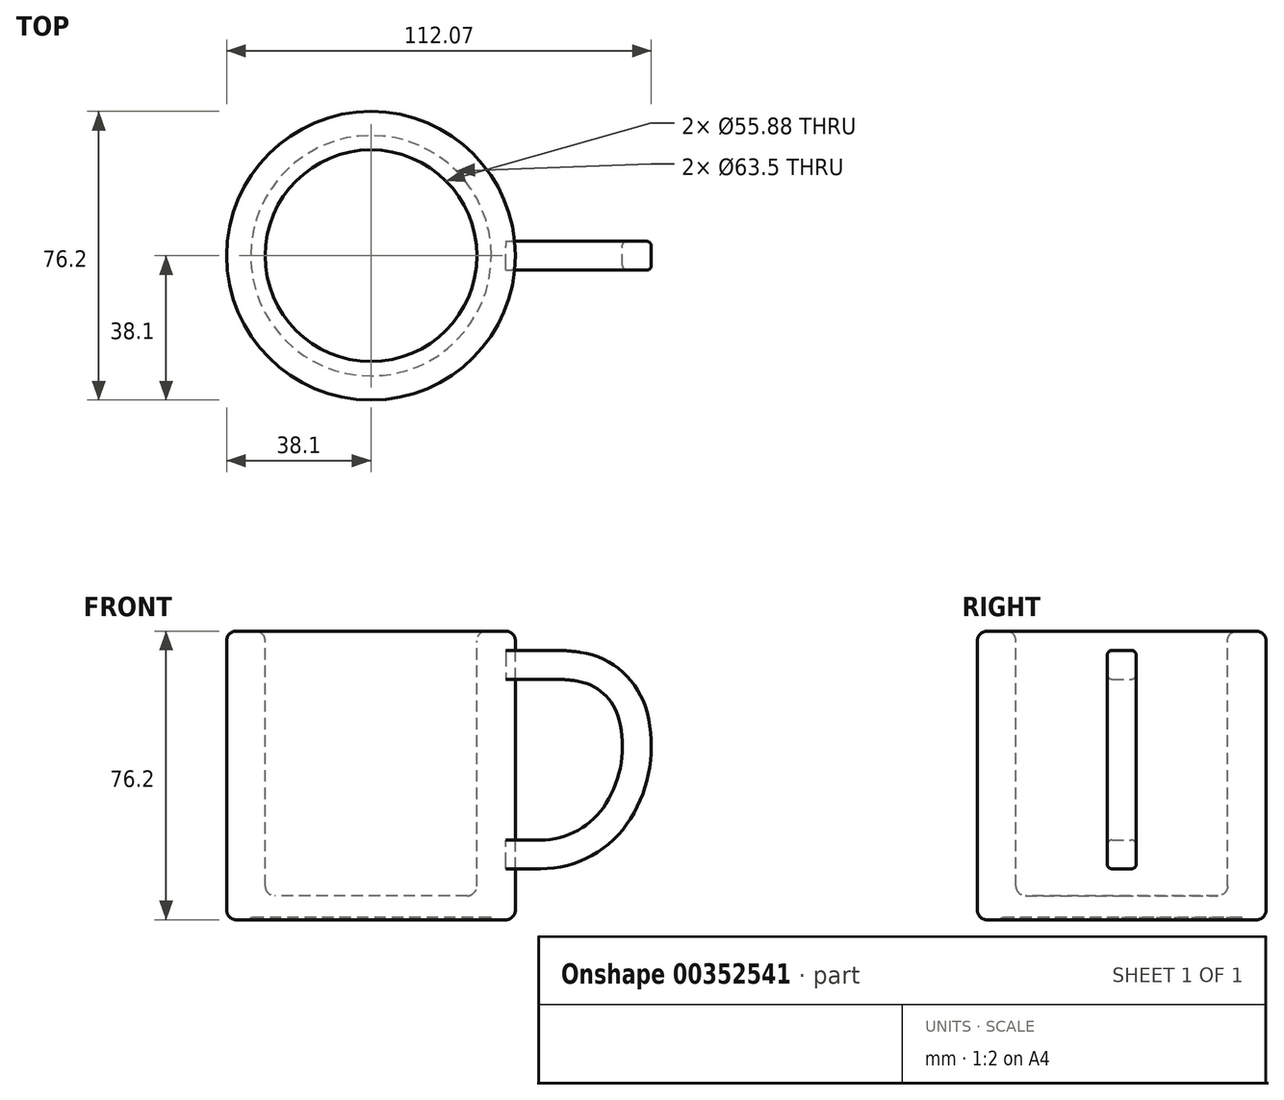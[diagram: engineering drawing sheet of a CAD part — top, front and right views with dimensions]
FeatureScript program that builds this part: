
annotation { "Feature Type Name" : "Feature", "Feature Type Description" : "" }
export const myFeature = defineFeature(function(context is Context, id is Id, definition is map)
    precondition{}
    {
        {
            var Q0;
            Q0=qCreatedBy(makeId("Front.planeOp"),FACE);
            var sketch = newSketch(context, id + "F0", { "sketchPlane" : qUnion([Q0])});
            skLineSegment(sketch, "E0.bottom", {"start": v(30.48, 76.2) * mm, "end": v(35.56, 76.2) * mm});
            skLineSegment(sketch, "E0.top", {"start": v(32, 0) * mm, "end": v(35.56, 0) * mm});
            skLineSegment(sketch, "E0.left", {"start": v(0, 6.35) * mm, "end": v(0, 0) * mm});
            skLineSegment(sketch, "E0.right", {"start": v(38.1, 73.66) * mm, "end": v(38.1, 2.54) * mm});
            skLineSegment(sketch, "E1.top", {"start": v(0, 6.35) * mm, "end": v(25.4, 6.35) * mm});
            skLineSegment(sketch, "E1.right", {"start": v(27.94, 73.66) * mm, "end": v(27.94, 8.9) * mm});
            skPoint(sketch, "E2.visualSharp", {"position": v(27.94, 6.35) * mm});
            skArc(sketch, "E2.filletArc", {"start": v(25.4, 6.35) * mm, "mid": v(27.2, 7.1) * mm, "end": v(27.94, 8.9) * mm});
            skPoint(sketch, "E3.visualSharp", {"position": v(27.94, 76.2) * mm});
            skArc(sketch, "E3.filletArc", {"start": v(30.48, 76.2) * mm, "mid": v(28.68, 75.46) * mm, "end": v(27.94, 73.66) * mm});
            skPoint(sketch, "E4.visualSharp", {"position": v(38.1, 76.2) * mm});
            skArc(sketch, "E4.filletArc", {"start": v(38.1, 73.66) * mm, "mid": v(37.36, 75.46) * mm, "end": v(35.56, 76.2) * mm});
            skPoint(sketch, "E5.visualSharp", {"position": v(38.1, 0) * mm});
            skArc(sketch, "E5.filletArc", {"start": v(35.56, 0) * mm, "mid": v(37.36, 0.74) * mm, "end": v(38.1, 2.54) * mm});
            skLineSegment(sketch, "E6.top", {"start": v(0, 0.64) * mm, "end": v(31.5, 0.64) * mm});
            skLineSegment(sketch, "E6.right", {"start": v(31.75, 0.25) * mm, "end": v(31.75, 0.38) * mm});
            skPoint(sketch, "E7.visualSharp", {"position": v(31.75, 0.64) * mm});
            skArc(sketch, "E7.filletArc", {"start": v(31.75, 0.38) * mm, "mid": v(31.67, 0.56) * mm, "end": v(31.5, 0.64) * mm});
            skPoint(sketch, "E8.visualSharp", {"position": v(31.75, 0) * mm});
            skArc(sketch, "E8.filletArc", {"start": v(31.75, 0.25) * mm, "mid": v(31.82, 0.07) * mm, "end": v(32, 0) * mm});
            skSolve(sketch);
        }
        {
            var Q0;
            Q0=makeQuery(id+"F0.imprint","IMPRINT",FACE,{"disambiguationData":[TD([[makeQuery(id+"F0.imprint","IMPRINT",EDGE,{"derivedFrom":sQuery(id+"F0.wireOp",EDGE,"E0.bottom")}),-1.0]])]});
            var Q1;
            Q1=sQuery(id+"F0.wireOp",EDGE,"E0.left");
            revolve(context, id + "F1", {"entities" : qUnion([Q0]), "axis" : qUnion([Q1]), "revolveType" : RevolveType.FULL});
        }
        {
            var Q0;
            Q0=qCreatedBy(makeId("Front.planeOp"),FACE);
            var sketch = newSketch(context, id + "F2", { "sketchPlane" : qUnion([Q0])});
            skLineSegment(sketch, "E9", {"start": v(35.56, 64.23) * mm, "end": v(48.44, 64.23) * mm});
            skLineSegment(sketch, "E10", {"start": v(44.7, 20.32) * mm, "end": v(35.56, 20.32) * mm});
            skArc(sketch, "E11", {"start": v(48.44, 64.23) * mm, "mid": v(51.37, 64.12) * mm, "end": v(54.3, 63.8) * mm});
            skArc(sketch, "E12", {"start": v(54.3, 63.8) * mm, "mid": v(61.86, 60.22) * mm, "end": v(66.17, 53.05) * mm});
            skArc(sketch, "E13", {"start": v(66.17, 53.05) * mm, "mid": v(66.73, 41.33) * mm, "end": v(62.66, 30.32) * mm});
            skArc(sketch, "E14", {"start": v(44.7, 20.32) * mm, "mid": v(54.98, 22.99) * mm, "end": v(62.66, 30.32) * mm});
            skSolve(sketch);
        }
        {
            var Q0;
            Q0=sQuery(id+"F2.wireOp",VERTEX,"E9.start");
            var Q1;
            Q1=qCreatedBy(makeId("Right.planeOp"),FACE);
            cPlane(context, id + "F3", {"entities" : qUnion([Q0, Q1]), "cplaneType" : CPlaneType.PLANE_POINT, "offset" : 25.4 * mm, "width" : 152.4 * mm, "height" : 152.4 * mm});
        }
        {
            var Q0;
            Q0=qCreatedBy(id+"F3.planeOp",FACE);
            var sketch = newSketch(context, id + "F4", { "sketchPlane" : qUnion([Q0])});
            skLineSegment(sketch, "E15.bottom", {"start": v(-2.54, 71.12) * mm, "end": v(2.54, 71.12) * mm});
            skLineSegment(sketch, "E15.top", {"start": v(-2.54, 63.5) * mm, "end": v(2.54, 63.5) * mm});
            skLineSegment(sketch, "E15.left", {"start": v(-3.81, 69.85) * mm, "end": v(-3.81, 64.77) * mm});
            skLineSegment(sketch, "E15.right", {"start": v(3.81, 69.85) * mm, "end": v(3.81, 64.77) * mm});
            skPoint(sketch, "E16.visualSharp", {"position": v(-3.81, 71.12) * mm});
            skArc(sketch, "E16.filletArc", {"start": v(-2.54, 71.12) * mm, "mid": v(-3.44, 70.75) * mm, "end": v(-3.81, 69.85) * mm});
            skPoint(sketch, "E17.visualSharp", {"position": v(3.81, 71.12) * mm});
            skArc(sketch, "E17.filletArc", {"start": v(3.81, 69.85) * mm, "mid": v(3.44, 70.75) * mm, "end": v(2.54, 71.12) * mm});
            skPoint(sketch, "E18.visualSharp", {"position": v(3.81, 63.5) * mm});
            skArc(sketch, "E18.filletArc", {"start": v(2.54, 63.5) * mm, "mid": v(3.44, 63.87) * mm, "end": v(3.8, 64.77) * mm});
            skPoint(sketch, "E19.visualSharp", {"position": v(-3.81, 63.5) * mm});
            skArc(sketch, "E19.filletArc", {"start": v(-3.8, 64.77) * mm, "mid": v(-3.44, 63.87) * mm, "end": v(-2.54, 63.5) * mm});
            skSolve(sketch);
        }
        {
            var Q0;
            Q0 = qSketchRegion(id + "F4", true);
            var Q1;
            Q1 = qConstructionFilter(qBodyType(qCreatedBy(id + "F2" ,EDGE), BodyType.WIRE), ConstructionObject.NO);
            sweep(context, id + "F5", {"profiles" : qUnion([Q0]), "path" : qUnion([Q1])});
        }
    });
